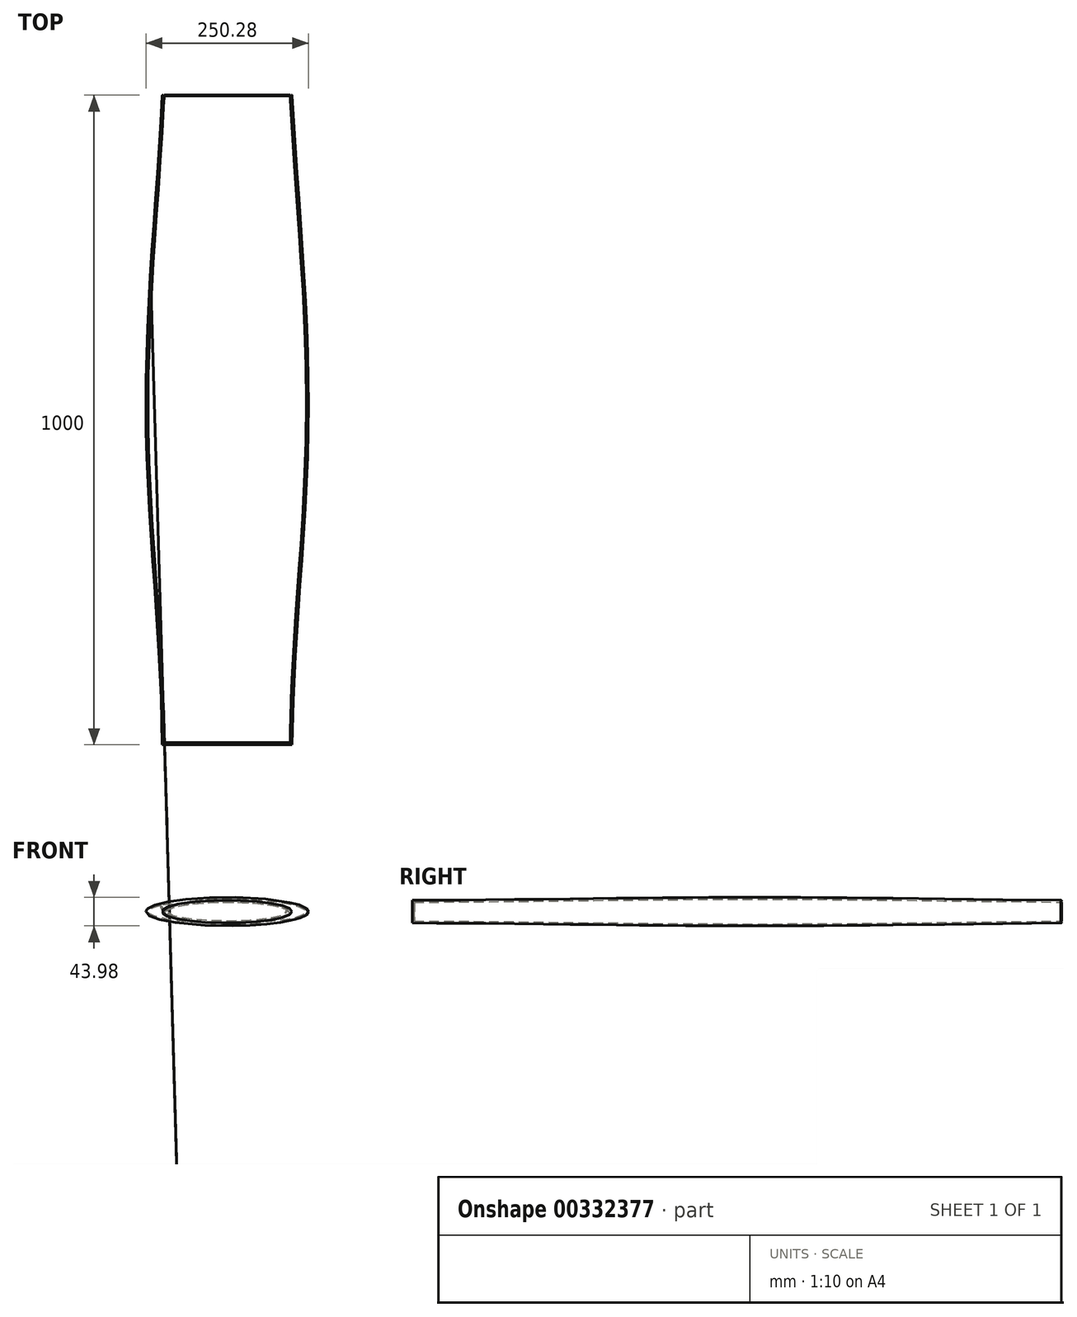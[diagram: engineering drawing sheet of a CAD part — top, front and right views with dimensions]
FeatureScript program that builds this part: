
annotation { "Feature Type Name" : "Feature", "Feature Type Description" : "" }
export const myFeature = defineFeature(function(context is Context, id is Id, definition is map)
    precondition{}
    {
        {
            var Q0;
            Q0=qCreatedBy(makeId("Front.planeOp"),FACE);
            cPlane(context, id + "F0", {"entities" : qUnion([Q0]), "cplaneType" : CPlaneType.OFFSET, "offset" : 500 * mm, "width" : 150 * mm, "height" : 150 * mm});
        }
        {
            var Q0;
            Q0=qCreatedBy(makeId("Front.planeOp"),FACE);
            cPlane(context, id + "F1", {"entities" : qUnion([Q0]), "cplaneType" : CPlaneType.OFFSET, "offset" : 500 * mm, "oppositeDirection" : true, "width" : 150 * mm, "height" : 150 * mm});
        }
        {
            var Q0;
            Q0=qCreatedBy(id+"F0.planeOp",FACE);
            var sketch = newSketch(context, id + "F2", { "sketchPlane" : qUnion([Q0])});
            skEllipse(sketch, "E0", {"center": v(0, 0) * mm, "majorRadius": 100 * mm, "minorRadius": 17.57 * mm, "majorAxis": v(1, 0)});
            skSolve(sketch);
        }
        {
            var Q0;
            Q0=qCreatedBy(makeId("Front.planeOp"),FACE);
            var sketch = newSketch(context, id + "F3", { "sketchPlane" : qUnion([Q0])});
            skEllipse(sketch, "E1", {"center": v(0, 0) * mm, "majorRadius": 125 * mm, "minorRadius": 21.97 * mm, "majorAxis": v(1, 0)});
            skSolve(sketch);
        }
        {
            var Q0;
            Q0=qCreatedBy(id+"F1.planeOp",FACE);
            var sketch = newSketch(context, id + "F4", { "sketchPlane" : qUnion([Q0])});
            skEllipse(sketch, "E2", {"center": v(0, 0) * mm, "majorRadius": 100 * mm, "minorRadius": 17.57 * mm, "majorAxis": v(1, 0)});
            skSolve(sketch);
        }
        {
            var Q0;
            Q0=makeQuery(id+"F2.imprint","IMPRINT",FACE,{"disambiguationData":[TD([[makeQuery(id+"F2.imprint","IMPRINT",EDGE,{"derivedFrom":sQuery(id+"F2.wireOp",EDGE,"E0")}),1.0]])]});
            var Q1;
            Q1=makeQuery(id+"F3.imprint","IMPRINT",FACE,{"disambiguationData":[TD([[makeQuery(id+"F3.imprint","IMPRINT",EDGE,{"derivedFrom":sQuery(id+"F3.wireOp",EDGE,"E1")}),1.0]])]});
            var Q2;
            Q2=makeQuery(id+"F4.imprint","IMPRINT",FACE,{"disambiguationData":[TD([[makeQuery(id+"F4.imprint","IMPRINT",EDGE,{"derivedFrom":sQuery(id+"F4.wireOp",EDGE,"E2")}),1.0]])]});
            loft(context, id + "F5", {"sheetProfilesArray" : [{ "sheetProfileEntities" : qUnion([Q0]) }, { "sheetProfileEntities" : qUnion([Q1]) }, { "sheetProfileEntities" : qUnion([Q2]) }]});
        }
        {
            var Q0;
            Q0=makeQuery(id+"F5.opLoft","CAP_FACE",FACE,{"disambiguationData":[OSD([makeQuery(id+"F4.imprint","IMPRINT",FACE,{"disambiguationData":[TD([[makeQuery(id+"F4.imprint","IMPRINT",EDGE,{"derivedFrom":sQuery(id+"F4.wireOp",EDGE,"E2")}),1.0]])]})])],"isStart":true});
            shell(context, id + "F6", {"entities" : qUnion([Q0]), "thickness" : 3 * mm});
        }
        {
            var Q0;
            Q0=makeQuery(id+"F5.opLoft","MID_CAP_EDGE",EDGE,{"disambiguationData":[OSD([sQuery(id+"F2.wireOp",EDGE,"E0"),sQuery(id+"F4.wireOp",EDGE,"E2")])],"capPos":2.0});
            fillet(context, id + "F7", {"entities" : qUnion([Q0]), "radius" : 1 * mm, "tangentPropagation" : true, "allowEdgeOverflow" : false});
        }
    });
